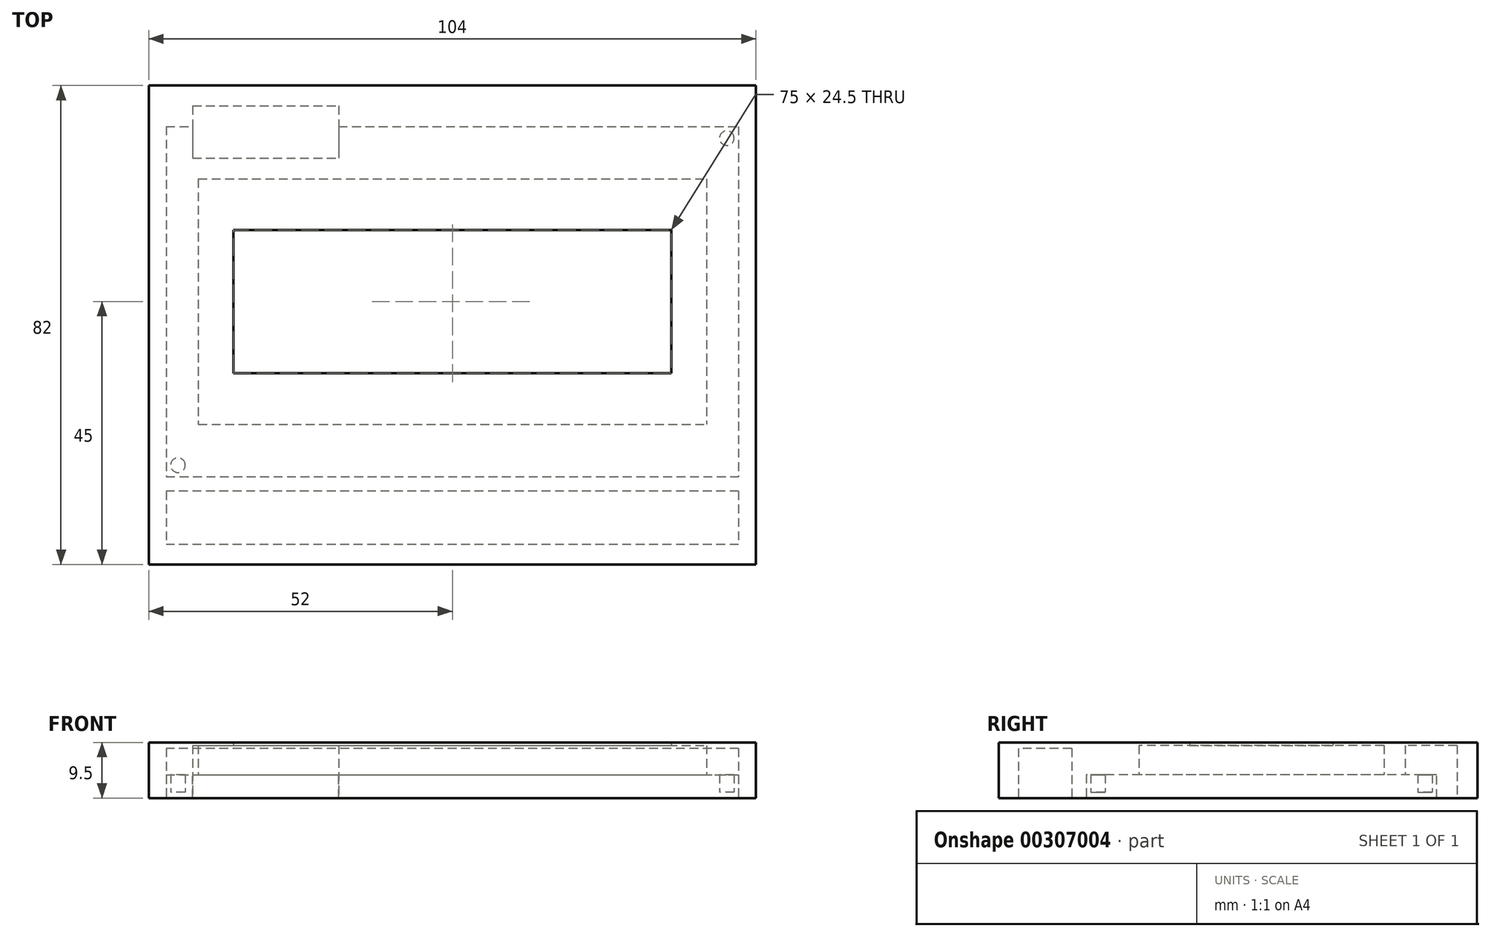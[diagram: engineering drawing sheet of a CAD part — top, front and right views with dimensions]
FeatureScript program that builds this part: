
annotation { "Feature Type Name" : "Feature", "Feature Type Description" : "" }
export const myFeature = defineFeature(function(context is Context, id is Id, definition is map)
    precondition{}
    {
        {
            var Q0;
            Q0=qCreatedBy(makeId("Top.planeOp"),FACE);
            var sketch = newSketch(context, id + "F0", { "sketchPlane" : qUnion([Q0])});
            skLineSegment(sketch, "E0.bottom", {"start": v(-37.5, -12.25) * mm, "end": v(37.5, -12.25) * mm});
            skLineSegment(sketch, "E0.top", {"start": v(-37.5, 12.25) * mm, "end": v(37.5, 12.25) * mm});
            skLineSegment(sketch, "E0.left", {"start": v(-37.5, -12.25) * mm, "end": v(-37.5, 12.25) * mm});
            skLineSegment(sketch, "E0.right", {"start": v(37.5, -12.25) * mm, "end": v(37.5, 12.25) * mm});
            skLineSegment(sketch, "E1", {"start": v(0, 149.04) * mm, "end": v(0, -150.96) * mm, "construction": true});
            skLineSegment(sketch, "E2", {"start": v(-149.52, 0) * mm, "end": v(148.56, 0) * mm, "construction": true});
            skLineSegment(sketch, "E3.bottom", {"start": v(-43.5, 21) * mm, "end": v(43.5, 21) * mm});
            skLineSegment(sketch, "E3.top", {"start": v(-43.5, -21) * mm, "end": v(43.5, -21) * mm});
            skLineSegment(sketch, "E3.left", {"start": v(-43.5, 21) * mm, "end": v(-43.5, -21) * mm});
            skLineSegment(sketch, "E3.right", {"start": v(43.5, 21) * mm, "end": v(43.5, -21) * mm});
            skLineSegment(sketch, "E4.bottom", {"start": v(-49, 30) * mm, "end": v(49, 30) * mm});
            skLineSegment(sketch, "E4.top", {"start": v(-49, -30) * mm, "end": v(49, -30) * mm});
            skLineSegment(sketch, "E4.left", {"start": v(-49, 30) * mm, "end": v(-49, -30) * mm});
            skLineSegment(sketch, "E4.right", {"start": v(49, 30) * mm, "end": v(49, -30) * mm});
            skCircle(sketch, "E5", {"center": v(-47, 28) * mm, "radius": 1.25 * mm});
            skCircle(sketch, "E6.MirrorC", {"center": v(47, 28) * mm, "radius": 1.25 * mm});
            skCircle(sketch, "E7.MirrorC", {"center": v(-47, -28) * mm, "radius": 1.25 * mm});
            skCircle(sketch, "E8.MirrorC", {"center": v(47, -28) * mm, "radius": 1.25 * mm});
            skLineSegment(sketch, "E9.bottom", {"start": v(-41.98, 27.1) * mm, "end": v(-21.98, 27.1) * mm});
            skLineSegment(sketch, "E9.top", {"start": v(-41.98, 30) * mm, "end": v(-21.98, 30) * mm});
            skLineSegment(sketch, "E9.left", {"start": v(-41.98, 27.1) * mm, "end": v(-41.98, 30) * mm});
            skLineSegment(sketch, "E9.right", {"start": v(-21.98, 27.1) * mm, "end": v(-21.98, 30) * mm});
            skSolve(sketch);
        }
        {
            var Q0;
            Q0=qCreatedBy(makeId("Top.planeOp"),FACE);
            var sketch = newSketch(context, id + "F1", { "sketchPlane" : qUnion([Q0])});
            skLineSegment(sketch, "E10.bottom", {"start": v(-52, 37) * mm, "end": v(52, 37) * mm});
            skLineSegment(sketch, "E10.top", {"start": v(-52, -45) * mm, "end": v(52, -45) * mm});
            skLineSegment(sketch, "E10.left", {"start": v(-52, 37) * mm, "end": v(-52, -45) * mm});
            skLineSegment(sketch, "E10.right", {"start": v(52, 37) * mm, "end": v(52, -45) * mm});
            skLineSegment(sketch, "E11.0", {"start": v(-43.5, 21) * mm, "end": v(-43.5, -21) * mm});
            skLineSegment(sketch, "E11.1", {"start": v(-43.5, -21) * mm, "end": v(43.5, -21) * mm});
            skLineSegment(sketch, "E11.2", {"start": v(43.5, 21) * mm, "end": v(43.5, -21) * mm});
            skLineSegment(sketch, "E11.3", {"start": v(-43.5, 21) * mm, "end": v(43.5, 21) * mm});
            skLineSegment(sketch, "E12.0", {"start": v(-37.5, 12.25) * mm, "end": v(37.5, 12.25) * mm});
            skLineSegment(sketch, "E12.1", {"start": v(-37.5, -12.25) * mm, "end": v(-37.5, 12.25) * mm});
            skLineSegment(sketch, "E12.2", {"start": v(-37.5, -12.25) * mm, "end": v(37.5, -12.25) * mm});
            skLineSegment(sketch, "E12.3", {"start": v(37.5, -12.25) * mm, "end": v(37.5, 12.25) * mm});
            skPoint(sketch, "E13.0", {"position": v(-47, -28) * mm});
            skPoint(sketch, "E13.1", {"position": v(47, -28) * mm});
            skPoint(sketch, "E13.2", {"position": v(47, 28) * mm});
            skPoint(sketch, "E13.3", {"position": v(-47, 28) * mm});
            skLineSegment(sketch, "E14.bottom", {"start": v(-44.48, 33.5) * mm, "end": v(-19.48, 33.5) * mm});
            skLineSegment(sketch, "E14.top", {"start": v(-44.48, 24.6) * mm, "end": v(-19.48, 24.6) * mm});
            skLineSegment(sketch, "E14.left", {"start": v(-44.48, 33.5) * mm, "end": v(-44.48, 24.6) * mm});
            skLineSegment(sketch, "E14.right", {"start": v(-19.48, 33.5) * mm, "end": v(-19.48, 24.6) * mm});
            skLineSegment(sketch, "E15.3.0", {"start": v(-21.98, 30) * mm, "end": v(-41.98, 30) * mm, "construction": true});
            skLineSegment(sketch, "E15.3.1", {"start": v(-41.98, 30) * mm, "end": v(-41.98, 27.1) * mm, "construction": true});
            skLineSegment(sketch, "E15.3.2", {"start": v(-41.98, 27.1) * mm, "end": v(-21.98, 27.1) * mm, "construction": true});
            skLineSegment(sketch, "E15.3.3", {"start": v(-21.98, 27.1) * mm, "end": v(-21.98, 30) * mm, "construction": true});
            skLineSegment(sketch, "E16.0", {"start": v(-49, 30) * mm, "end": v(49, 30) * mm});
            skLineSegment(sketch, "E16.1", {"start": v(49, 30) * mm, "end": v(49, -30) * mm});
            skLineSegment(sketch, "E16.2", {"start": v(-49, -30) * mm, "end": v(49, -30) * mm});
            skLineSegment(sketch, "E16.3", {"start": v(-49, 30) * mm, "end": v(-49, -30) * mm});
            skSolve(sketch);
        }
        {
            var Q0;
            Q0=makeQuery(id+"F1.imprint","IMPRINT",FACE,{"disambiguationData":[TD([[makeQuery(id+"F1.imprint","IMPRINT",EDGE,{"derivedFrom":sQuery(id+"F1.wireOp",EDGE,"E10.bottom")}),-1.0]])]});
            var Q1;
            Q1=makeQuery(id+"F1.imprint","IMPRINT",FACE,{"disambiguationData":[TD([[makeQuery(id+"F1.imprint","IMPRINT",EDGE,{"derivedFrom":sQuery(id+"F1.wireOp",EDGE,"E14.bottom")}),-1.0]])]});
            var Q2;
            Q2=makeQuery(id+"F1.imprint","IMPRINT",FACE,{"disambiguationData":[TD([[makeQuery(id+"F1.imprint","IMPRINT",EDGE,{"derivedFrom":sQuery(id+"F1.wireOp",EDGE,"E11.0")}),1.0]])]});
            var Q3;
            Q3=makeQuery(id+"F1.imprint","IMPRINT",FACE,{"disambiguationData":[TD([[makeQuery(id+"F1.imprint","IMPRINT",EDGE,{"derivedFrom":sQuery(id+"F1.wireOp",EDGE,"E11.0")}),-1.0]])]});
            var Q4;
            {var subQ0=sQuery(id+"F1.wireOp",EDGE,"E14.top");Q4=makeQuery(id+"F1.imprint","IMPRINT",FACE,{"disambiguationData":[TD([[makeQuery(id+"F1.imprint","IMPRINT",EDGE,{"derivedFrom":subQ0}),1.0]])]});}
            extrude(context, id + "F2", {"entities" : qUnion([Q0, Q1, Q2, Q3, Q4]), "depth" : 9.5 * mm});
        }
        {
            var Q0;
            Q0=makeQuery(id+"F1.imprint","IMPRINT",FACE,{"disambiguationData":[TD([[makeQuery(id+"F1.imprint","IMPRINT",EDGE,{"derivedFrom":sQuery(id+"F1.wireOp",EDGE,"E11.0")}),1.0]])]});
            var Q1;
            {var subQ0=sQuery(id+"F1.wireOp",EDGE,"E14.top");Q1=makeQuery(id+"F1.imprint","IMPRINT",FACE,{"disambiguationData":[TD([[makeQuery(id+"F1.imprint","IMPRINT",EDGE,{"derivedFrom":subQ0}),1.0]])]});}
            var Q2;
            {var subQ0=sQuery(id+"F1.wireOp",EDGE,"E14.bottom");Q2=makeQuery(id+"F1.imprint","IMPRINT",FACE,{"disambiguationData":[TD([[makeQuery(id+"F1.imprint","IMPRINT",EDGE,{"derivedFrom":subQ0}),-1.0]])]});}
            extrude(context, id + "F3", {"entities" : qUnion([Q0, Q1, Q2]), "operationType" : NewBodyOperationType.REMOVE, "depth" : 9 * mm});
        }
        {
            var Q0;
            Q0=makeQuery(id+"F1.imprint","IMPRINT",FACE,{"disambiguationData":[TD([[makeQuery(id+"F1.imprint","IMPRINT",EDGE,{"derivedFrom":sQuery(id+"F1.wireOp",EDGE,"E11.0")}),-1.0]])]});
            var Q1;
            Q1=makeQuery(id+"F1.imprint","IMPRINT",FACE,{"disambiguationData":[TD([[makeQuery(id+"F1.imprint","IMPRINT",EDGE,{"derivedFrom":sQuery(id+"F1.wireOp",EDGE,"E11.0")}),1.0]])]});
            var Q2;
            {var subQ0=sQuery(id+"F1.wireOp",EDGE,"E14.top");Q2=makeQuery(id+"F1.imprint","IMPRINT",FACE,{"disambiguationData":[TD([[makeQuery(id+"F1.imprint","IMPRINT",EDGE,{"derivedFrom":subQ0}),1.0]])]});}
            var Q3;
            Q3=sQuery(id+"F1.wireOp",EDGE,"E16.0");
            var Q4;
            Q4=sQuery(id+"F1.wireOp",EDGE,"E16.1");
            var Q5;
            Q5=sQuery(id+"F1.wireOp",EDGE,"E16.2");
            extrude(context, id + "F4", {"entities" : qUnion([Q0, Q1, Q2]), "operationType" : NewBodyOperationType.REMOVE, "surfaceEntities" : qUnion([Q3, Q4, Q5]), "depth" : 1 * mm});
        }
        {
            var Q0;
            Q0=makeQuery(id+"F0.imprint","IMPRINT",FACE,{"disambiguationData":[TD([[makeQuery(id+"F0.imprint","IMPRINT",EDGE,{"derivedFrom":sQuery(id+"F0.wireOp",EDGE,"E5")}),1.0]])]});
            var Q1;
            Q1=makeQuery(id+"F0.imprint","IMPRINT",FACE,{"disambiguationData":[TD([[makeQuery(id+"F0.imprint","IMPRINT",EDGE,{"derivedFrom":sQuery(id+"F0.wireOp",EDGE,"E6.MirrorC")}),-1.0]])]});
            var Q2;
            Q2=makeQuery(id+"F0.imprint","IMPRINT",FACE,{"disambiguationData":[TD([[makeQuery(id+"F0.imprint","IMPRINT",EDGE,{"derivedFrom":sQuery(id+"F0.wireOp",EDGE,"E8.MirrorC")}),1.0]])]});
            var Q3;
            Q3=makeQuery(id+"F0.imprint","IMPRINT",FACE,{"disambiguationData":[TD([[makeQuery(id+"F0.imprint","IMPRINT",EDGE,{"derivedFrom":sQuery(id+"F0.wireOp",EDGE,"E7.MirrorC")}),-1.0]])]});
            var Q4;
            Q4=makeQuery(id+"F4.boolean.opBoolean","COPY",FACE,{"derivedFrom":makeQuery(id+"F4.opExtrude","CAP_FACE",FACE,{"disambiguationData":[OSD([sQuery(id+"F1.wireOp",EDGE,"E12.0"),sQuery(id+"F1.wireOp",EDGE,"E12.1"),sQuery(id+"F1.wireOp",EDGE,"E12.2"),sQuery(id+"F1.wireOp",EDGE,"E12.3"),sQuery(id+"F1.wireOp",EDGE,"E16.0"),sQuery(id+"F1.wireOp",EDGE,"E16.1"),sQuery(id+"F1.wireOp",EDGE,"E16.2"),sQuery(id+"F1.wireOp",EDGE,"E16.3")])],"isStart":false})});
            extrude(context, id + "F5", {"entities" : qUnion([Q0, Q1, Q2, Q3]), "operationType" : NewBodyOperationType.REMOVE, "endBoundEntityFace" : qUnion([Q4]), "depth" : 4 * mm});
        }
        {
            var Q0;
            Q0=makeQuery(id+"F2.opExtrude","CAP_FACE",FACE,{"disambiguationData":[OSD([sQuery(id+"F1.wireOp",EDGE,"E10.bottom"),sQuery(id+"F1.wireOp",EDGE,"E10.top"),sQuery(id+"F1.wireOp",EDGE,"E10.left"),sQuery(id+"F1.wireOp",EDGE,"E10.right"),sQuery(id+"F1.wireOp",EDGE,"E12.0"),sQuery(id+"F1.wireOp",EDGE,"E12.1"),sQuery(id+"F1.wireOp",EDGE,"E12.2"),sQuery(id+"F1.wireOp",EDGE,"E12.3")])],"isStart":true});
            var sketch = newSketch(context, id + "F6", { "sketchPlane" : qUnion([Q0])});
            skLineSegment(sketch, "E17.bottom", {"start": v(49, 32.46) * mm, "end": v(-49, 32.46) * mm});
            skLineSegment(sketch, "E17.top", {"start": v(49, 41.6) * mm, "end": v(-49, 41.6) * mm});
            skLineSegment(sketch, "E17.left", {"start": v(49, 32.46) * mm, "end": v(49, 41.6) * mm});
            skLineSegment(sketch, "E17.right", {"start": v(-49, 32.46) * mm, "end": v(-49, 41.6) * mm});
            skSolve(sketch);
        }
        {
            var Q0;
            Q0 = qSketchRegion(id + "F6", true);
            var Q1;
            Q1=makeQuery(id+"F3.boolean.opBoolean","COPY",FACE,{"derivedFrom":makeQuery(id+"F3.opExtrude","CAP_FACE",FACE,{"disambiguationData":[OSD([sQuery(id+"F1.wireOp",EDGE,"E11.0"),sQuery(id+"F1.wireOp",EDGE,"E11.1"),sQuery(id+"F1.wireOp",EDGE,"E11.2"),sQuery(id+"F1.wireOp",EDGE,"E11.3"),sQuery(id+"F1.wireOp",EDGE,"E12.0"),sQuery(id+"F1.wireOp",EDGE,"E12.1"),sQuery(id+"F1.wireOp",EDGE,"E12.2"),sQuery(id+"F1.wireOp",EDGE,"E12.3")])],"isStart":false})});
            extrude(context, id + "F7", {"entities" : qUnion([Q0]), "operationType" : NewBodyOperationType.REMOVE, "oppositeDirection" : true, "endBoundEntityFace" : qUnion([Q1]), "depth" : 8.5 * mm});
        }
    });
